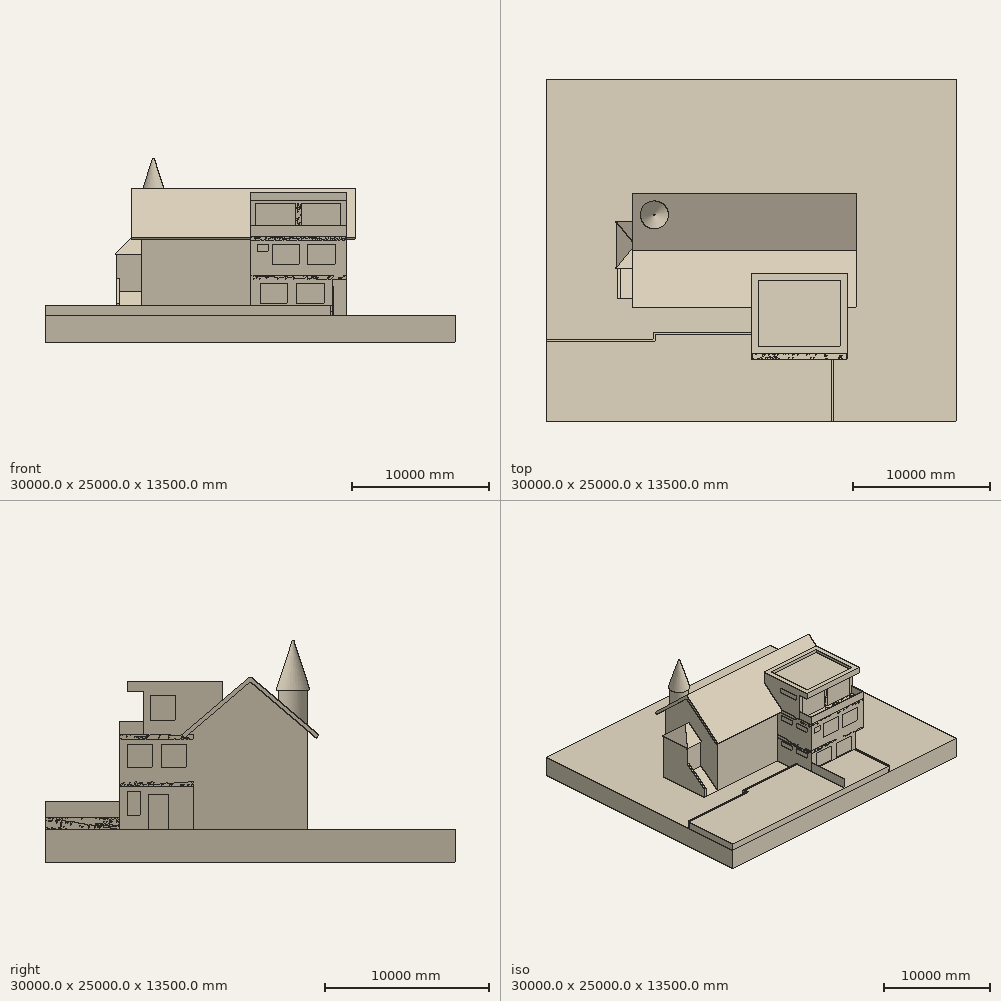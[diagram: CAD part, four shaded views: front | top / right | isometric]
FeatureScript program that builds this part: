
annotation { "Feature Type Name" : "Feature", "Feature Type Description" : "" }
export const myFeature = defineFeature(function(context is Context, id is Id, definition is map)
    precondition{}
    {
        {
            var Q0;
            Q0=qCreatedBy(makeId("Top.planeOp"),FACE);
            var sketch = newSketch(context, id + "F0", { "sketchPlane" : qUnion([Q0])});
            skLineSegment(sketch, "E0.bottom", {"start": v(-7000, 3500) * mm, "end": v(7000, 3500) * mm});
            skLineSegment(sketch, "E0.top", {"start": v(-7000, -3500) * mm, "end": v(7000, -3500) * mm});
            skLineSegment(sketch, "E0.left", {"start": v(-7000, 3500) * mm, "end": v(-7000, -3500) * mm});
            skLineSegment(sketch, "E0.right", {"start": v(7000, 3500) * mm, "end": v(7000, -3500) * mm});
            skPoint(sketch, "E0.middle", {"position": v(0, 0) * mm});
            skSolve(sketch);
        }
        {
            var Q0;
            Q0=makeQuery(id+"F0.imprint","IMPRINT",FACE,{"disambiguationData":[TD([[makeQuery(id+"F0.imprint","IMPRINT",EDGE,{"derivedFrom":sQuery(id+"F0.wireOp",EDGE,"E0.bottom")}),-1.0]])]});
            extrude(context, id + "F1", {"entities" : qUnion([Q0]), "depth" : 6000 * mm});
        }
        {
            var Q0;
            Q0=makeQuery(id+"F1.opExtrude","SWEPT_FACE",FACE,{"disambiguationData":[OSD([sQuery(id+"F0.wireOp",EDGE,"E0.left")])]});
            var sketch = newSketch(context, id + "F2", { "sketchPlane" : qUnion([Q0])});
            skLineSegment(sketch, "E1", {"start": v(0, 6000) * mm, "end": v(0, 8988.26) * mm});
            skPoint(sketch, "E1.endSnap0", {"position": v(0, 6000) * mm});
            skLineSegment(sketch, "E2", {"start": v(0, 8988.26) * mm, "end": v(-3500, 6000) * mm});
            skLineSegment(sketch, "E3", {"start": v(0, 8988.26) * mm, "end": v(3500, 6000) * mm});
            skSolve(sketch);
        }
        {
            var Q0;
            {var subQ0=sQuery(id+"F2.wireOp",EDGE,"E1");Q0=makeQuery(id+"F2.imprint","IMPRINT",FACE,{"disambiguationData":[TD([[makeQuery(id+"F2.imprint","IMPRINT",EDGE,{"derivedFrom":subQ0}),1.0]])]});}
            var Q1;
            {var subQ0=sQuery(id+"F2.wireOp",EDGE,"E1");Q1=makeQuery(id+"F2.imprint","IMPRINT",FACE,{"disambiguationData":[TD([[makeQuery(id+"F2.imprint","IMPRINT",EDGE,{"derivedFrom":subQ0}),-1.0]])]});}
            extrude(context, id + "F3", {"entities" : qUnion([Q0, Q1]), "operationType" : NewBodyOperationType.ADD, "oppositeDirection" : true, "depth" : 14000 * mm});
        }
        {
            var Q0;
            Q0=makeQuery(id+"F3.opExtrude","SWEPT_FACE",FACE,{"disambiguationData":[OSD([sQuery(id+"F2.wireOp",EDGE,"E2")])]});
            extrude(context, id + "F4", {"entities" : qUnion([Q0]), "operationType" : NewBodyOperationType.ADD, "endBound" : BoundingType.SYMMETRIC, "depth" : 500 * mm});
        }
        {
            var Q0;
            Q0=makeQuery(id+"F3.opExtrude","SWEPT_FACE",FACE,{"disambiguationData":[OSD([sQuery(id+"F2.wireOp",EDGE,"E3")])]});
            extrude(context, id + "F5", {"entities" : qUnion([Q0]), "operationType" : NewBodyOperationType.ADD, "endBound" : BoundingType.SYMMETRIC, "depth" : 500 * mm});
        }
        {
            var Q0;
            {var subQ0=sQuery(id+"F2.wireOp",EDGE,"E3");var subQ1=sQuery(id+"F2.wireOp",EDGE,"E2");var subQ2=sQuery(id+"F0.wireOp",EDGE,"E0.left");Q0=makeQuery(id+"F5.boolean.opBoolean","MERGE",FACE,{"derivedFrom":[makeQuery(id+"F4.boolean.opBoolean","MERGE",FACE,{"derivedFrom":[makeQuery(id+"F3.boolean.opBoolean","MERGE",FACE,{"derivedFrom":[makeQuery(id+"F1.opExtrude","SWEPT_FACE",FACE,{"disambiguationData":[OSD([subQ2])]}),makeQuery(id+"F3.opExtrude","CAP_FACE",FACE,{"disambiguationData":[OSD([subQ2,subQ1,subQ0])],"isStart":true})]}),makeQuery(id+"F4.opExtrude","SWEPT_FACE",FACE,{"disambiguationData":[OSD([subQ1]),TDD([makeQuery(id+"F3.opExtrude","CAP_EDGE",EDGE,{"disambiguationData":[OSD([subQ1])],"isStart":true})])]})]}),makeQuery(id+"F5.opExtrude","SWEPT_FACE",FACE,{"disambiguationData":[OSD([subQ0]),TDD([makeQuery(id+"F3.opExtrude","CAP_EDGE",EDGE,{"disambiguationData":[OSD([subQ0])],"isStart":true})])]})]});}
            var sketch = newSketch(context, id + "F6", { "sketchPlane" : qUnion([Q0])});
            skLineSegment(sketch, "E4", {"start": v(-162.33, 9178.39) * mm, "end": v(0, 9316.98) * mm});
            skLineSegment(sketch, "E5", {"start": v(0, 9316.98) * mm, "end": v(162.33, 9178.39) * mm});
            skSolve(sketch);
        }
        {
            var Q0;
            Q0=makeQuery(id+"F6.imprint","IMPRINT",FACE,{"disambiguationData":[TD([[makeQuery(id+"F6.imprint","IMPRINT",EDGE,{"derivedFrom":sQuery(id+"F6.wireOp",EDGE,"E4")}),-1.0]])]});
            extrude(context, id + "F7", {"entities" : qUnion([Q0]), "operationType" : NewBodyOperationType.ADD, "oppositeDirection" : true, "depth" : 14000 * mm});
        }
        {
            var Q0;
            Q0=makeQuery(id+"F4.opExtrude","SWEPT_FACE",FACE,{"disambiguationData":[OSD([sQuery(id+"F0.wireOp",EDGE,"E0.bottom"),sQuery(id+"F0.wireOp",EDGE,"E0.left"),sQuery(id+"F2.wireOp",EDGE,"E2")])]});
            extrude(context, id + "F8", {"entities" : qUnion([Q0]), "operationType" : NewBodyOperationType.ADD, "depth" : 700 * mm});
        }
        {
            var Q0;
            Q0=makeQuery(id+"F5.opExtrude","SWEPT_FACE",FACE,{"disambiguationData":[OSD([sQuery(id+"F0.wireOp",EDGE,"E0.top"),sQuery(id+"F0.wireOp",EDGE,"E0.left"),sQuery(id+"F2.wireOp",EDGE,"E3")])]});
            extrude(context, id + "F9", {"entities" : qUnion([Q0]), "operationType" : NewBodyOperationType.ADD, "depth" : 700 * mm});
        }
        {
            var Q0;
            {var subQ0=sQuery(id+"F2.wireOp",EDGE,"E3");var subQ1=sQuery(id+"F0.wireOp",EDGE,"E0.left");var subQ2=sQuery(id+"F0.wireOp",EDGE,"E0.top");var subQ3=sQuery(id+"F2.wireOp",EDGE,"E2");var subQ4=sQuery(id+"F0.wireOp",EDGE,"E0.bottom");Q0=makeQuery(id+"F9.boolean.opBoolean","MERGE",FACE,{"derivedFrom":[makeQuery(id+"F8.boolean.opBoolean","MERGE",FACE,{"derivedFrom":[makeQuery(id+"F7.boolean.opBoolean","MERGE",FACE,{"derivedFrom":[makeQuery(id+"F5.boolean.opBoolean","MERGE",FACE,{"derivedFrom":[makeQuery(id+"F4.boolean.opBoolean","MERGE",FACE,{"derivedFrom":[makeQuery(id+"F3.boolean.opBoolean","MERGE",FACE,{"derivedFrom":[makeQuery(id+"F1.opExtrude","SWEPT_FACE",FACE,{"disambiguationData":[OSD([subQ1])]}),makeQuery(id+"F3.opExtrude","CAP_FACE",FACE,{"disambiguationData":[OSD([subQ1,subQ3,subQ0])],"isStart":true})]}),makeQuery(id+"F4.opExtrude","SWEPT_FACE",FACE,{"disambiguationData":[OSD([subQ3]),TDD([makeQuery(id+"F3.opExtrude","CAP_EDGE",EDGE,{"disambiguationData":[OSD([subQ3])],"isStart":true})])]})]}),makeQuery(id+"F5.opExtrude","SWEPT_FACE",FACE,{"disambiguationData":[OSD([subQ0]),TDD([makeQuery(id+"F3.opExtrude","CAP_EDGE",EDGE,{"disambiguationData":[OSD([subQ0])],"isStart":true})])]})]}),makeQuery(id+"F7.opExtrude","CAP_FACE",FACE,{"disambiguationData":[OSD([sQuery(id+"F2.wireOp",EDGE,"E1"),subQ3,subQ0,sQuery(id+"F6.wireOp",EDGE,"E4"),sQuery(id+"F6.wireOp",EDGE,"E5")])],"isStart":true})]}),makeQuery(id+"F8.opExtrude","SWEPT_FACE",FACE,{"disambiguationData":[OSD([subQ4,subQ1,subQ3]),TDD([makeQuery(id+"F4.opExtrude","SWEPT_EDGE",EDGE,{"disambiguationData":[OSD([subQ4,subQ1,subQ3])]})])]})]}),makeQuery(id+"F9.opExtrude","SWEPT_FACE",FACE,{"disambiguationData":[OSD([subQ2,subQ1,subQ0]),TDD([makeQuery(id+"F5.opExtrude","SWEPT_EDGE",EDGE,{"disambiguationData":[OSD([subQ2,subQ1,subQ0])]})])]})]});}
            var sketch = newSketch(context, id + "F10", { "sketchPlane" : qUnion([Q0])});
            skLineSegment(sketch, "E6", {"start": v(-3500, 6000) * mm, "end": v(0, 8917.56) * mm});
            skLineSegment(sketch, "E7", {"start": v(0, 8917.56) * mm, "end": v(3500, 6000) * mm});
            skSolve(sketch);
        }
        {
            var Q0;
            Q0=makeQuery(id+"F10.imprint","IMPRINT",FACE,{"disambiguationData":[TD([[makeQuery(id+"F10.imprint","IMPRINT",EDGE,{"derivedFrom":sQuery(id+"F10.wireOp",EDGE,"E6")}),1.0]])]});
            extrude(context, id + "F11", {"entities" : qUnion([Q0]), "operationType" : NewBodyOperationType.ADD, "depth" : 700 * mm});
        }
        {
            var Q0;
            {var subQ0=sQuery(id+"F2.wireOp",EDGE,"E3");var subQ1=sQuery(id+"F0.wireOp",EDGE,"E0.right");var subQ2=sQuery(id+"F0.wireOp",EDGE,"E0.left");var subQ3=sQuery(id+"F2.wireOp",EDGE,"E2");Q0=makeQuery(id+"F9.boolean.opBoolean","MERGE",FACE,{"derivedFrom":[makeQuery(id+"F8.boolean.opBoolean","MERGE",FACE,{"derivedFrom":[makeQuery(id+"F7.boolean.opBoolean","MERGE",FACE,{"derivedFrom":[makeQuery(id+"F5.boolean.opBoolean","MERGE",FACE,{"derivedFrom":[makeQuery(id+"F4.boolean.opBoolean","MERGE",FACE,{"derivedFrom":[makeQuery(id+"F3.boolean.opBoolean","MERGE",FACE,{"derivedFrom":[makeQuery(id+"F1.opExtrude","SWEPT_FACE",FACE,{"disambiguationData":[OSD([subQ1])]}),makeQuery(id+"F3.opExtrude","CAP_FACE",FACE,{"disambiguationData":[OSD([subQ2,subQ3,subQ0])],"isStart":false})]}),makeQuery(id+"F4.opExtrude","SWEPT_FACE",FACE,{"disambiguationData":[OSD([subQ3]),TDD([makeQuery(id+"F3.opExtrude","CAP_EDGE",EDGE,{"disambiguationData":[OSD([subQ3])],"isStart":false})])]})]}),makeQuery(id+"F5.opExtrude","SWEPT_FACE",FACE,{"disambiguationData":[OSD([subQ0]),TDD([makeQuery(id+"F3.opExtrude","CAP_EDGE",EDGE,{"disambiguationData":[OSD([subQ0])],"isStart":false})])]})]}),makeQuery(id+"F7.opExtrude","CAP_FACE",FACE,{"disambiguationData":[OSD([sQuery(id+"F2.wireOp",EDGE,"E1"),subQ3,subQ0,sQuery(id+"F6.wireOp",EDGE,"E4"),sQuery(id+"F6.wireOp",EDGE,"E5")])],"isStart":false})]}),makeQuery(id+"F8.opExtrude","SWEPT_FACE",FACE,{"disambiguationData":[OSD([sQuery(id+"F0.wireOp",EDGE,"E0.bottom"),subQ2,subQ1,subQ3])]})]}),makeQuery(id+"F9.opExtrude","SWEPT_FACE",FACE,{"disambiguationData":[OSD([sQuery(id+"F0.wireOp",EDGE,"E0.top"),subQ2,subQ1,subQ0])]})]});}
            var sketch = newSketch(context, id + "F12", { "sketchPlane" : qUnion([Q0])});
            skLineSegment(sketch, "E8", {"start": v(-3500, 6000) * mm, "end": v(0, 8988.26) * mm});
            skLineSegment(sketch, "E9", {"start": v(0, 8988.26) * mm, "end": v(3500, 6000) * mm});
            skSolve(sketch);
        }
        {
            var Q0;
            Q0=makeQuery(id+"F12.imprint","IMPRINT",FACE,{"disambiguationData":[TD([[makeQuery(id+"F12.imprint","IMPRINT",EDGE,{"derivedFrom":sQuery(id+"F12.wireOp",EDGE,"E8")}),1.0]])]});
            extrude(context, id + "F13", {"entities" : qUnion([Q0]), "operationType" : NewBodyOperationType.ADD, "depth" : 700 * mm});
        }
        {
            var Q0;
            Q0=makeQuery(id+"F1.opExtrude","CAP_FACE",FACE,{"disambiguationData":[OSD([sQuery(id+"F0.wireOp",EDGE,"E0.bottom"),sQuery(id+"F0.wireOp",EDGE,"E0.top"),sQuery(id+"F0.wireOp",EDGE,"E0.left"),sQuery(id+"F0.wireOp",EDGE,"E0.right")])],"isStart":true});
            var sketch = newSketch(context, id + "F14", { "sketchPlane" : qUnion([Q0])});
            skLineSegment(sketch, "E10", {"start": v(7000, 3500) * mm, "end": v(0, 3500) * mm});
            skLineSegment(sketch, "E11", {"start": v(0, 3500) * mm, "end": v(0, 8000) * mm});
            skLineSegment(sketch, "E12", {"start": v(0, 8000) * mm, "end": v(7000, 8000) * mm});
            skLineSegment(sketch, "E13", {"start": v(7000, 8000) * mm, "end": v(7000, 3500) * mm});
            skSolve(sketch);
        }
        {
            var Q0;
            Q0=makeQuery(id+"F14.imprint","IMPRINT",FACE,{"disambiguationData":[TD([[makeQuery(id+"F14.imprint","IMPRINT",EDGE,{"derivedFrom":sQuery(id+"F14.wireOp",EDGE,"E10")}),1.0]])]});
            extrude(context, id + "F15", {"entities" : qUnion([Q0]), "operationType" : NewBodyOperationType.ADD, "oppositeDirection" : true, "depth" : 9000 * mm});
        }
        {
            var Q0;
            Q0=makeQuery(id+"F15.opExtrude","SWEPT_FACE",FACE,{"disambiguationData":[OSD([sQuery(id+"F14.wireOp",EDGE,"E10")])]});
            extrude(context, id + "F16", {"entities" : qUnion([Q0]), "operationType" : NewBodyOperationType.ADD, "depth" : 1800 * mm});
        }
        {
            var Q0;
            Q0=makeQuery(id+"F15.opExtrude","SWEPT_FACE",FACE,{"disambiguationData":[OSD([sQuery(id+"F14.wireOp",EDGE,"E12")])]});
            var sketch = newSketch(context, id + "F17", { "sketchPlane" : qUnion([Q0])});
            skLineSegment(sketch, "E14", {"start": v(0, 8400) * mm, "end": v(7000, 8400) * mm});
            skLineSegment(sketch, "E15", {"start": v(7000, 8400) * mm, "end": v(7000, 5800) * mm});
            skLineSegment(sketch, "E16", {"start": v(7000, 5800) * mm, "end": v(0, 5800) * mm});
            skLineSegment(sketch, "E17", {"start": v(0, 5800) * mm, "end": v(0, 8400) * mm});
            skSolve(sketch);
        }
        {
            var Q0;
            Q0=makeQuery(id+"F17.imprint","IMPRINT",FACE,{"disambiguationData":[TD([[makeQuery(id+"F17.imprint","IMPRINT",EDGE,{"derivedFrom":sQuery(id+"F17.wireOp",EDGE,"E14")}),-1.0]])]});
            extrude(context, id + "F18", {"entities" : qUnion([Q0]), "operationType" : NewBodyOperationType.REMOVE, "oppositeDirection" : true, "depth" : 1500 * mm, "offsetDistance" : 25 * mm});
        }
        {
            var Q0;
            {var subQ7=sQuery(id+"F14.wireOp",EDGE,"E10");var subQ8=sQuery(id+"F14.wireOp",EDGE,"E12");Q0=makeQuery(id+"F18.boolean.opBoolean","SPLIT",FACE,{"disambiguationData":[TD([makeQuery(id+"F16.opExtrude","SWEPT_FACE",FACE,{"disambiguationData":[OSD([subQ7])]})])],"derivedFrom":makeQuery(id+"F15.opExtrude","SWEPT_FACE",FACE,{"disambiguationData":[OSD([subQ8])]})});}
            extrude(context, id + "F19", {"entities" : qUnion([Q0]), "operationType" : NewBodyOperationType.REMOVE, "oppositeDirection" : true, "depth" : 500 * mm, "offsetDistance" : 25 * mm});
        }
        {
            var Q0;
            {var subQ0=sQuery(id+"F14.wireOp",EDGE,"E10");Q0=makeQuery(id+"F16.boolean.opBoolean","MERGE",FACE,{"derivedFrom":[makeQuery(id+"F15.opExtrude","CAP_FACE",FACE,{"disambiguationData":[OSD([subQ0,sQuery(id+"F14.wireOp",EDGE,"E11"),sQuery(id+"F14.wireOp",EDGE,"E12"),sQuery(id+"F14.wireOp",EDGE,"E13")])],"isStart":false}),makeQuery(id+"F16.opExtrude","SWEPT_FACE",FACE,{"disambiguationData":[OSD([subQ0])]})]});}
            var sketch = newSketch(context, id + "F20", { "sketchPlane" : qUnion([Q0])});
            skLineSegment(sketch, "E18", {"start": v(500, -2200) * mm, "end": v(500, -7000) * mm});
            skLineSegment(sketch, "E19", {"start": v(500, -7000) * mm, "end": v(6500, -7000) * mm});
            skLineSegment(sketch, "E20", {"start": v(6500, -7000) * mm, "end": v(6500, -2200) * mm});
            skLineSegment(sketch, "E21", {"start": v(6500, -2200) * mm, "end": v(500, -2200) * mm});
            skSolve(sketch);
        }
        {
            var Q0;
            Q0=makeQuery(id+"F20.imprint","IMPRINT",FACE,{"disambiguationData":[TD([[makeQuery(id+"F20.imprint","IMPRINT",EDGE,{"derivedFrom":sQuery(id+"F20.wireOp",EDGE,"E18")}),1.0]])]});
            extrude(context, id + "F21", {"entities" : qUnion([Q0]), "operationType" : NewBodyOperationType.REMOVE, "oppositeDirection" : true, "depth" : 300 * mm});
        }
        {
            var Q0;
            {var subQ1=sQuery(id+"F14.wireOp",EDGE,"E12");Q0=makeQuery(id+"F18.boolean.opBoolean","SPLIT",FACE,{"disambiguationData":[TD([makeQuery(id+"F18.opExtrude","SWEPT_FACE",FACE,{"disambiguationData":[OSD([sQuery(id+"F17.wireOp",EDGE,"E16")])]})])],"derivedFrom":makeQuery(id+"F15.opExtrude","SWEPT_FACE",FACE,{"disambiguationData":[OSD([subQ1])]})});}
            var sketch = newSketch(context, id + "F22", { "sketchPlane" : qUnion([Q0])});
            skLineSegment(sketch, "E22", {"start": v(0, 0) * mm, "end": v(7000, 0) * mm});
            skLineSegment(sketch, "E23", {"start": v(7000, 0) * mm, "end": v(7000, 2600) * mm});
            skLineSegment(sketch, "E24", {"start": v(7000, 2600) * mm, "end": v(0, 2600) * mm});
            skLineSegment(sketch, "E25", {"start": v(0, 2600) * mm, "end": v(0, 0) * mm});
            skLineSegment(sketch, "E26", {"start": v(0, 2600) * mm, "end": v(0, 2900) * mm});
            skLineSegment(sketch, "E27", {"start": v(7000, 2900) * mm, "end": v(7000, 2600) * mm});
            skLineSegment(sketch, "E28", {"start": v(0, 2900) * mm, "end": v(0, 5800) * mm});
            skLineSegment(sketch, "E29", {"start": v(0, 2900) * mm, "end": v(7000, 2900) * mm});
            skLineSegment(sketch, "E30", {"start": v(0, 2900) * mm, "end": v(0, 5500) * mm});
            skLineSegment(sketch, "E31", {"start": v(0, 5500) * mm, "end": v(7000, 5500) * mm});
            skLineSegment(sketch, "E32", {"start": v(7000, 5500) * mm, "end": v(7000, 2900) * mm});
            skLineSegment(sketch, "E33", {"start": v(0, 5800) * mm, "end": v(7000, 5800) * mm});
            skLineSegment(sketch, "E34", {"start": v(7000, 5800) * mm, "end": v(7000, 5500) * mm});
            skLineSegment(sketch, "E35", {"start": v(0, 5500) * mm, "end": v(0, 5800) * mm});
            skSolve(sketch);
        }
        {
            var Q0;
            Q0=makeQuery(id+"F22.imprint","IMPRINT",FACE,{"disambiguationData":[TD([[makeQuery(id+"F22.imprint","IMPRINT",EDGE,{"derivedFrom":sQuery(id+"F22.wireOp",EDGE,"E24")}),-1.0]])]});
            extrude(context, id + "F23", {"entities" : qUnion([Q0]), "oppositeDirection" : true, "depth" : 4500 * mm});
        }
        {
            var Q0;
            Q0=makeQuery(id+"F22.imprint","IMPRINT",FACE,{"disambiguationData":[TD([[makeQuery(id+"F22.imprint","IMPRINT",EDGE,{"derivedFrom":sQuery(id+"F22.wireOp",EDGE,"E31")}),1.0]])]});
            extrude(context, id + "F24", {"entities" : qUnion([Q0]), "oppositeDirection" : true, "depth" : 4500 * mm});
        }
        {
            var Q0;
            Q0=makeQuery(id+"F18.boolean.opBoolean","COPY",FACE,{"derivedFrom":makeQuery(id+"F18.opExtrude","SWEPT_FACE",FACE,{"disambiguationData":[OSD([sQuery(id+"F17.wireOp",EDGE,"E16")])]})});
            var sketch = newSketch(context, id + "F25", { "sketchPlane" : qUnion([Q0])});
            skLineSegment(sketch, "E36", {"start": v(40, -7960) * mm, "end": v(6960, -7960) * mm});
            skLineSegment(sketch, "E37", {"start": v(6960, -7960) * mm, "end": v(6960, -6500) * mm});
            skLineSegment(sketch, "E38", {"start": v(40, -6500) * mm, "end": v(40, -7960) * mm});
            skSolve(sketch);
        }
        {
            var Q0;
            Q0=makeQuery(id+"F25.imprint","IMPRINT",FACE,{"disambiguationData":[TD([[makeQuery(id+"F25.imprint","IMPRINT",EDGE,{"derivedFrom":sQuery(id+"F25.wireOp",EDGE,"E36")}),-1.0]])]});
            extrude(context, id + "F26", {"entities" : qUnion([Q0]), "depth" : 800 * mm});
        }
        {
            var Q0;
            {var subQ0=sQuery(id+"F14.wireOp",EDGE,"E13");var subQ1=sQuery(id+"F0.wireOp",EDGE,"E0.right");var subQ2=sQuery(id+"F2.wireOp",EDGE,"E3");var subQ3=sQuery(id+"F0.wireOp",EDGE,"E0.left");var subQ4=sQuery(id+"F2.wireOp",EDGE,"E2");Q0=makeQuery(id+"F16.boolean.opBoolean","MERGE",FACE,{"derivedFrom":[makeQuery(id+"F15.boolean.opBoolean","MERGE",FACE,{"derivedFrom":[makeQuery(id+"F9.boolean.opBoolean","MERGE",FACE,{"derivedFrom":[makeQuery(id+"F8.boolean.opBoolean","MERGE",FACE,{"derivedFrom":[makeQuery(id+"F7.boolean.opBoolean","MERGE",FACE,{"derivedFrom":[makeQuery(id+"F5.boolean.opBoolean","MERGE",FACE,{"derivedFrom":[makeQuery(id+"F4.boolean.opBoolean","MERGE",FACE,{"derivedFrom":[makeQuery(id+"F3.boolean.opBoolean","MERGE",FACE,{"derivedFrom":[makeQuery(id+"F1.opExtrude","SWEPT_FACE",FACE,{"disambiguationData":[OSD([subQ1])]}),makeQuery(id+"F3.opExtrude","CAP_FACE",FACE,{"disambiguationData":[OSD([subQ3,subQ4,subQ2])],"isStart":false})]}),makeQuery(id+"F4.opExtrude","SWEPT_FACE",FACE,{"disambiguationData":[OSD([subQ4]),TDD([makeQuery(id+"F3.opExtrude","CAP_EDGE",EDGE,{"disambiguationData":[OSD([subQ4])],"isStart":false})])]})]}),makeQuery(id+"F5.opExtrude","SWEPT_FACE",FACE,{"disambiguationData":[OSD([subQ2]),TDD([makeQuery(id+"F3.opExtrude","CAP_EDGE",EDGE,{"disambiguationData":[OSD([subQ2])],"isStart":false})])]})]}),makeQuery(id+"F7.opExtrude","CAP_FACE",FACE,{"disambiguationData":[OSD([sQuery(id+"F2.wireOp",EDGE,"E1"),subQ4,subQ2,sQuery(id+"F6.wireOp",EDGE,"E4"),sQuery(id+"F6.wireOp",EDGE,"E5")])],"isStart":false})]}),makeQuery(id+"F8.opExtrude","SWEPT_FACE",FACE,{"disambiguationData":[OSD([sQuery(id+"F0.wireOp",EDGE,"E0.bottom"),subQ3,subQ1,subQ4])]})]}),makeQuery(id+"F9.opExtrude","SWEPT_FACE",FACE,{"disambiguationData":[OSD([sQuery(id+"F0.wireOp",EDGE,"E0.top"),subQ3,subQ1,subQ2])]})]}),makeQuery(id+"F15.opExtrude","SWEPT_FACE",FACE,{"disambiguationData":[OSD([subQ0])]})]}),makeQuery(id+"F16.opExtrude","SWEPT_FACE",FACE,{"disambiguationData":[OSD([subQ1,sQuery(id+"F14.wireOp",EDGE,"E10"),subQ0])]})]});}
            var sketch = newSketch(context, id + "F27", { "sketchPlane" : qUnion([Q0])});
            skLineSegment(sketch, "E39", {"start": v(-8000, 0) * mm, "end": v(-8000, 2600.45) * mm});
            skLineSegment(sketch, "E40", {"start": v(-8000, 2600.45) * mm, "end": v(-3500, 2600.45) * mm});
            skLineSegment(sketch, "E41", {"start": v(-3500, 2600.45) * mm, "end": v(-3500, 0) * mm});
            skLineSegment(sketch, "E42", {"start": v(-3500, 0) * mm, "end": v(-8000, 0) * mm});
            skSolve(sketch);
        }
        {
            var Q0;
            Q0=makeQuery(id+"F27.imprint","IMPRINT",FACE,{"disambiguationData":[TD([[makeQuery(id+"F27.imprint","IMPRINT",EDGE,{"derivedFrom":sQuery(id+"F27.wireOp",EDGE,"E39")}),1.0]])]});
            extrude(context, id + "F28", {"entities" : qUnion([Q0]), "operationType" : NewBodyOperationType.REMOVE, "oppositeDirection" : true, "depth" : 1000 * mm});
        }
        {
            var Q0;
            {var subQ0=sQuery(id+"F27.wireOp",EDGE,"E40");var subQ1=sQuery(id+"F14.wireOp",EDGE,"E12");var subQ2=sQuery(id+"F27.wireOp",EDGE,"E41");Q0=makeQuery(id+"F28.boolean.opBoolean","COPY",FACE,{"disambiguationData":[TD([makeQuery(id+"F15.opExtrude","SWEPT_FACE",FACE,{"disambiguationData":[OSD([subQ1])]})])],"derivedFrom":makeQuery(id+"F28.opExtrude","CAP_FACE",FACE,{"disambiguationData":[OSD([sQuery(id+"F27.wireOp",EDGE,"E39"),subQ0,subQ2,sQuery(id+"F27.wireOp",EDGE,"E42")])],"isStart":false})});}
            var sketch = newSketch(context, id + "F29", { "sketchPlane" : qUnion([Q0])});
            skLineSegment(sketch, "E43", {"start": v(-6200, 0) * mm, "end": v(-6200, 2100) * mm});
            skLineSegment(sketch, "E44", {"start": v(-6200, 2100) * mm, "end": v(-5000, 2100) * mm});
            skLineSegment(sketch, "E45", {"start": v(-5000, 2100) * mm, "end": v(-5000, 0) * mm});
            skLineSegment(sketch, "E46", {"start": v(-5000, 0) * mm, "end": v(-6200, 0) * mm});
            skSolve(sketch);
        }
        {
            var Q0;
            Q0=makeQuery(id+"F29.imprint","IMPRINT",FACE,{"disambiguationData":[TD([[makeQuery(id+"F29.imprint","IMPRINT",EDGE,{"derivedFrom":sQuery(id+"F29.wireOp",EDGE,"E43")}),-1.0]])]});
            extrude(context, id + "F30", {"entities" : qUnion([Q0]), "endBound" : BoundingType.SYMMETRIC, "oppositeDirection" : true, "depth" : 100 * mm});
        }
        {
            var Q0;
            Q0=makeQuery(id+"F18.boolean.opBoolean","COPY",FACE,{"derivedFrom":makeQuery(id+"F18.opExtrude","CAP_FACE",FACE,{"disambiguationData":[OSD([sQuery(id+"F17.wireOp",EDGE,"E14"),sQuery(id+"F17.wireOp",EDGE,"E15"),sQuery(id+"F17.wireOp",EDGE,"E16"),sQuery(id+"F17.wireOp",EDGE,"E17")])],"isStart":false})});
            var sketch = newSketch(context, id + "F31", { "sketchPlane" : qUnion([Q0])});
            skLineSegment(sketch, "E47", {"start": v(348.69, 8181.2) * mm, "end": v(6584.02, 8181.2) * mm});
            skLineSegment(sketch, "E48", {"start": v(6584.02, 8181.2) * mm, "end": v(6584.02, 5800) * mm});
            skLineSegment(sketch, "E49", {"start": v(6584.02, 5800) * mm, "end": v(348.69, 5800) * mm});
            skLineSegment(sketch, "E50", {"start": v(348.69, 5800) * mm, "end": v(348.69, 8181.2) * mm});
            skSolve(sketch);
        }
        {
            var Q0;
            Q0 = qSketchRegion(id + "F31", true);
            extrude(context, id + "F32", {"entities" : qUnion([Q0]), "endBound" : BoundingType.SYMMETRIC, "oppositeDirection" : true, "depth" : 100 * mm});
        }
        {
            var Q0;
            Q0=makeQuery(id+"F18.boolean.opBoolean","COPY",FACE,{"derivedFrom":makeQuery(id+"F18.opExtrude","CAP_FACE",FACE,{"disambiguationData":[OSD([sQuery(id+"F17.wireOp",EDGE,"E14"),sQuery(id+"F17.wireOp",EDGE,"E15"),sQuery(id+"F17.wireOp",EDGE,"E16"),sQuery(id+"F17.wireOp",EDGE,"E17")])],"isStart":false})});
            var sketch = newSketch(context, id + "F33", { "sketchPlane" : qUnion([Q0])});
            skLineSegment(sketch, "E51", {"start": v(3300, 8400) * mm, "end": v(3300, 5800) * mm});
            skLineSegment(sketch, "E52", {"start": v(3300, 5800) * mm, "end": v(3700, 5800) * mm});
            skLineSegment(sketch, "E53", {"start": v(3700, 5800) * mm, "end": v(3700, 8400) * mm});
            skLineSegment(sketch, "E54", {"start": v(3700, 8400) * mm, "end": v(3300, 8400) * mm});
            skSolve(sketch);
        }
        {
            var Q0;
            Q0 = qSketchRegion(id + "F33", true);
            extrude(context, id + "F34", {"entities" : qUnion([Q0]), "operationType" : NewBodyOperationType.REMOVE, "depth" : 500 * mm});
        }
        {
            var Q0;
            {var subQ0=sQuery(id+"F14.wireOp",EDGE,"E11");Q0=makeQuery(id+"F16.boolean.opBoolean","MERGE",FACE,{"derivedFrom":[makeQuery(id+"F15.opExtrude","SWEPT_FACE",FACE,{"disambiguationData":[OSD([subQ0])]}),makeQuery(id+"F16.opExtrude","SWEPT_FACE",FACE,{"disambiguationData":[OSD([sQuery(id+"F0.wireOp",EDGE,"E0.top"),sQuery(id+"F14.wireOp",EDGE,"E10"),subQ0])]})]});}
            var sketch = newSketch(context, id + "F35", { "sketchPlane" : qUnion([Q0])});
            skLineSegment(sketch, "E55", {"start": v(6000, 2400) * mm, "end": v(7500, 2400) * mm});
            skLineSegment(sketch, "E56", {"start": v(7500, 2400) * mm, "end": v(7500, 1900) * mm});
            skLineSegment(sketch, "E57", {"start": v(7500, 1900) * mm, "end": v(6000, 1900) * mm});
            skLineSegment(sketch, "E58", {"start": v(6000, 1900) * mm, "end": v(6000, 2400) * mm});
            skLineSegment(sketch, "E59", {"start": v(5500, 2400) * mm, "end": v(4000, 2400) * mm});
            skLineSegment(sketch, "E60", {"start": v(4000, 2400) * mm, "end": v(4000, 1900) * mm});
            skLineSegment(sketch, "E61", {"start": v(4000, 1900) * mm, "end": v(5500, 1900) * mm});
            skLineSegment(sketch, "E62", {"start": v(5500, 1900) * mm, "end": v(5500, 2400) * mm});
            skSolve(sketch);
        }
        {
            var Q0;
            Q0=makeQuery(id+"F35.imprint","IMPRINT",FACE,{"disambiguationData":[TD([[makeQuery(id+"F35.imprint","IMPRINT",EDGE,{"derivedFrom":sQuery(id+"F35.wireOp",EDGE,"E55")}),-1.0]])]});
            var Q1;
            Q1=makeQuery(id+"F35.imprint","IMPRINT",FACE,{"disambiguationData":[TD([[makeQuery(id+"F35.imprint","IMPRINT",EDGE,{"derivedFrom":sQuery(id+"F35.wireOp",EDGE,"E59")}),1.0]])]});
            extrude(context, id + "F36", {"entities" : qUnion([Q0, Q1]), "endBound" : BoundingType.SYMMETRIC, "depth" : 10 * mm});
        }
        {
            var Q0;
            {var subQ1=sQuery(id+"F14.wireOp",EDGE,"E12");Q0=makeQuery(id+"F18.boolean.opBoolean","SPLIT",FACE,{"disambiguationData":[TD([makeQuery(id+"F18.opExtrude","SWEPT_FACE",FACE,{"disambiguationData":[OSD([sQuery(id+"F17.wireOp",EDGE,"E16")])]})])],"derivedFrom":makeQuery(id+"F15.opExtrude","SWEPT_FACE",FACE,{"disambiguationData":[OSD([subQ1])]})});}
            var sketch = newSketch(context, id + "F37", { "sketchPlane" : qUnion([Q0])});
            skLineSegment(sketch, "E63", {"start": v(700, 2350) * mm, "end": v(2700, 2350) * mm});
            skLineSegment(sketch, "E64", {"start": v(2700, 2350) * mm, "end": v(2700, 850) * mm});
            skLineSegment(sketch, "E65", {"start": v(2700, 850) * mm, "end": v(700, 850) * mm});
            skLineSegment(sketch, "E66", {"start": v(700, 850) * mm, "end": v(700, 2350) * mm});
            skLineSegment(sketch, "E67", {"start": v(3400, 2350) * mm, "end": v(5400, 2350) * mm});
            skLineSegment(sketch, "E68", {"start": v(5400, 2350) * mm, "end": v(5400, 850) * mm});
            skLineSegment(sketch, "E69", {"start": v(5400, 850) * mm, "end": v(3400, 850) * mm});
            skLineSegment(sketch, "E70", {"start": v(3400, 850) * mm, "end": v(3400, 2350) * mm});
            skSolve(sketch);
        }
        {
            var Q0;
            Q0 = qSketchRegion(id + "F37", true);
            extrude(context, id + "F38", {"entities" : qUnion([Q0]), "endBound" : BoundingType.SYMMETRIC, "depth" : 10 * mm});
        }
        {
            var Q0;
            {var subQ0=sQuery(id+"F14.wireOp",EDGE,"E11");Q0=makeQuery(id+"F16.boolean.opBoolean","MERGE",FACE,{"derivedFrom":[makeQuery(id+"F15.opExtrude","SWEPT_FACE",FACE,{"disambiguationData":[OSD([subQ0])]}),makeQuery(id+"F16.opExtrude","SWEPT_FACE",FACE,{"disambiguationData":[OSD([sQuery(id+"F0.wireOp",EDGE,"E0.top"),sQuery(id+"F14.wireOp",EDGE,"E10"),subQ0])]})]});}
            var sketch = newSketch(context, id + "F39", { "sketchPlane" : qUnion([Q0])});
            skLineSegment(sketch, "E71", {"start": v(4000, 5200) * mm, "end": v(4000, 4700) * mm});
            skLineSegment(sketch, "E72", {"start": v(4000, 4700) * mm, "end": v(5500, 4700) * mm});
            skLineSegment(sketch, "E73", {"start": v(5500, 4700) * mm, "end": v(5500, 5200) * mm});
            skLineSegment(sketch, "E74", {"start": v(5500, 5200) * mm, "end": v(4000, 5200) * mm});
            skLineSegment(sketch, "E75", {"start": v(6000, 5200) * mm, "end": v(6000, 4700) * mm});
            skLineSegment(sketch, "E76", {"start": v(6000, 4700) * mm, "end": v(7500, 4700) * mm});
            skLineSegment(sketch, "E77", {"start": v(7500, 4700) * mm, "end": v(7500, 5200) * mm});
            skLineSegment(sketch, "E78", {"start": v(7500, 5200) * mm, "end": v(6000, 5200) * mm});
            skSolve(sketch);
        }
        {
            var Q0;
            Q0 = qSketchRegion(id + "F39", true);
            extrude(context, id + "F40", {"entities" : qUnion([Q0]), "endBound" : BoundingType.SYMMETRIC, "depth" : 10 * mm});
        }
        {
            var Q0;
            {var subQ0=sQuery(id+"F27.wireOp",EDGE,"E40");var subQ1=sQuery(id+"F14.wireOp",EDGE,"E12");var subQ2=sQuery(id+"F27.wireOp",EDGE,"E41");Q0=makeQuery(id+"F28.boolean.opBoolean","COPY",FACE,{"disambiguationData":[TD([makeQuery(id+"F15.opExtrude","SWEPT_FACE",FACE,{"disambiguationData":[OSD([subQ1])]})])],"derivedFrom":makeQuery(id+"F28.opExtrude","CAP_FACE",FACE,{"disambiguationData":[OSD([sQuery(id+"F27.wireOp",EDGE,"E39"),subQ0,subQ2,sQuery(id+"F27.wireOp",EDGE,"E42")])],"isStart":false})});}
            var sketch = newSketch(context, id + "F41", { "sketchPlane" : qUnion([Q0])});
            skLineSegment(sketch, "E79", {"start": v(-7500, 2300.45) * mm, "end": v(-6700, 2300.45) * mm});
            skLineSegment(sketch, "E80", {"start": v(-6700, 2300.45) * mm, "end": v(-6700, 850) * mm});
            skLineSegment(sketch, "E81", {"start": v(-6700, 850) * mm, "end": v(-7500, 850) * mm});
            skLineSegment(sketch, "E82", {"start": v(-7500, 850) * mm, "end": v(-7500, 2300.45) * mm});
            skSolve(sketch);
        }
        {
            var Q0;
            Q0=makeQuery(id+"F41.imprint","IMPRINT",FACE,{"disambiguationData":[TD([[makeQuery(id+"F41.imprint","IMPRINT",EDGE,{"derivedFrom":sQuery(id+"F41.wireOp",EDGE,"E79")}),-1.0]])]});
            extrude(context, id + "F42", {"entities" : qUnion([Q0]), "endBound" : BoundingType.SYMMETRIC, "oppositeDirection" : true, "depth" : 10 * mm});
        }
        {
            var Q0;
            {var subQ1=sQuery(id+"F14.wireOp",EDGE,"E12");Q0=makeQuery(id+"F18.boolean.opBoolean","SPLIT",FACE,{"disambiguationData":[TD([makeQuery(id+"F18.opExtrude","SWEPT_FACE",FACE,{"disambiguationData":[OSD([sQuery(id+"F17.wireOp",EDGE,"E16")])]})])],"derivedFrom":makeQuery(id+"F15.opExtrude","SWEPT_FACE",FACE,{"disambiguationData":[OSD([subQ1])]})});}
            var sketch = newSketch(context, id + "F43", { "sketchPlane" : qUnion([Q0])});
            skLineSegment(sketch, "E83", {"start": v(500, 5200) * mm, "end": v(1300, 5200) * mm});
            skLineSegment(sketch, "E84", {"start": v(1300, 5200) * mm, "end": v(1300, 4700) * mm});
            skLineSegment(sketch, "E85", {"start": v(1300, 4700) * mm, "end": v(500, 4700) * mm});
            skLineSegment(sketch, "E86", {"start": v(500, 4700) * mm, "end": v(500, 5200) * mm});
            skLineSegment(sketch, "E87", {"start": v(1600, 5200) * mm, "end": v(1600, 3750) * mm});
            skLineSegment(sketch, "E88", {"start": v(1600, 3750) * mm, "end": v(3600, 3750) * mm});
            skLineSegment(sketch, "E89", {"start": v(3600, 3750) * mm, "end": v(3600, 5200) * mm});
            skLineSegment(sketch, "E90", {"start": v(3600, 5200) * mm, "end": v(1600, 5200) * mm});
            skLineSegment(sketch, "E91", {"start": v(4200, 5170.16) * mm, "end": v(6200, 5170.16) * mm});
            skLineSegment(sketch, "E92", {"start": v(6200, 5170.16) * mm, "end": v(6200, 3750) * mm});
            skLineSegment(sketch, "E93", {"start": v(6200, 3750) * mm, "end": v(4200, 3750) * mm});
            skLineSegment(sketch, "E94", {"start": v(4200, 3750) * mm, "end": v(4200, 5170.16) * mm});
            skSolve(sketch);
        }
        {
            var Q0;
            Q0 = qSketchRegion(id + "F43", true);
            extrude(context, id + "F44", {"entities" : qUnion([Q0]), "endBound" : BoundingType.SYMMETRIC, "depth" : 10 * mm});
        }
        {
            var Q0;
            {var subQ0=sQuery(id+"F14.wireOp",EDGE,"E13");var subQ1=sQuery(id+"F0.wireOp",EDGE,"E0.right");var subQ2=sQuery(id+"F2.wireOp",EDGE,"E3");var subQ3=sQuery(id+"F0.wireOp",EDGE,"E0.left");var subQ4=sQuery(id+"F2.wireOp",EDGE,"E2");Q0=makeQuery(id+"F16.boolean.opBoolean","MERGE",FACE,{"derivedFrom":[makeQuery(id+"F15.boolean.opBoolean","MERGE",FACE,{"derivedFrom":[makeQuery(id+"F9.boolean.opBoolean","MERGE",FACE,{"derivedFrom":[makeQuery(id+"F8.boolean.opBoolean","MERGE",FACE,{"derivedFrom":[makeQuery(id+"F7.boolean.opBoolean","MERGE",FACE,{"derivedFrom":[makeQuery(id+"F5.boolean.opBoolean","MERGE",FACE,{"derivedFrom":[makeQuery(id+"F4.boolean.opBoolean","MERGE",FACE,{"derivedFrom":[makeQuery(id+"F3.boolean.opBoolean","MERGE",FACE,{"derivedFrom":[makeQuery(id+"F1.opExtrude","SWEPT_FACE",FACE,{"disambiguationData":[OSD([subQ1])]}),makeQuery(id+"F3.opExtrude","CAP_FACE",FACE,{"disambiguationData":[OSD([subQ3,subQ4,subQ2])],"isStart":false})]}),makeQuery(id+"F4.opExtrude","SWEPT_FACE",FACE,{"disambiguationData":[OSD([subQ4]),TDD([makeQuery(id+"F3.opExtrude","CAP_EDGE",EDGE,{"disambiguationData":[OSD([subQ4])],"isStart":false})])]})]}),makeQuery(id+"F5.opExtrude","SWEPT_FACE",FACE,{"disambiguationData":[OSD([subQ2]),TDD([makeQuery(id+"F3.opExtrude","CAP_EDGE",EDGE,{"disambiguationData":[OSD([subQ2])],"isStart":false})])]})]}),makeQuery(id+"F7.opExtrude","CAP_FACE",FACE,{"disambiguationData":[OSD([sQuery(id+"F2.wireOp",EDGE,"E1"),subQ4,subQ2,sQuery(id+"F6.wireOp",EDGE,"E4"),sQuery(id+"F6.wireOp",EDGE,"E5")])],"isStart":false})]}),makeQuery(id+"F8.opExtrude","SWEPT_FACE",FACE,{"disambiguationData":[OSD([sQuery(id+"F0.wireOp",EDGE,"E0.bottom"),subQ3,subQ1,subQ4])]})]}),makeQuery(id+"F9.opExtrude","SWEPT_FACE",FACE,{"disambiguationData":[OSD([sQuery(id+"F0.wireOp",EDGE,"E0.top"),subQ3,subQ1,subQ2])]})]}),makeQuery(id+"F15.opExtrude","SWEPT_FACE",FACE,{"disambiguationData":[OSD([subQ0])]})]}),makeQuery(id+"F16.opExtrude","SWEPT_FACE",FACE,{"disambiguationData":[OSD([subQ1,sQuery(id+"F14.wireOp",EDGE,"E10"),subQ0])]})]});}
            var sketch = newSketch(context, id + "F45", { "sketchPlane" : qUnion([Q0])});
            skLineSegment(sketch, "E95", {"start": v(-7500, 5200) * mm, "end": v(-6000, 5200) * mm});
            skLineSegment(sketch, "E96", {"start": v(-6000, 5200) * mm, "end": v(-6000, 3750) * mm});
            skLineSegment(sketch, "E97", {"start": v(-6000, 3750) * mm, "end": v(-7500, 3750) * mm});
            skLineSegment(sketch, "E98", {"start": v(-7500, 3750) * mm, "end": v(-7500, 5200) * mm});
            skLineSegment(sketch, "E99", {"start": v(-5400, 5200) * mm, "end": v(-3900, 5200) * mm});
            skLineSegment(sketch, "E100", {"start": v(-3900, 5200) * mm, "end": v(-3900, 3750) * mm});
            skLineSegment(sketch, "E101", {"start": v(-3900, 3750) * mm, "end": v(-5400, 3750) * mm});
            skLineSegment(sketch, "E102", {"start": v(-5400, 3750) * mm, "end": v(-5400, 5200) * mm});
            skSolve(sketch);
        }
        {
            var Q0;
            Q0 = qSketchRegion(id + "F45", true);
            extrude(context, id + "F46", {"entities" : qUnion([Q0]), "endBound" : BoundingType.SYMMETRIC, "depth" : 10 * mm});
        }
        {
            var Q0;
            {var subQ0=sQuery(id+"F14.wireOp",EDGE,"E13");var subQ1=sQuery(id+"F0.wireOp",EDGE,"E0.right");var subQ2=sQuery(id+"F2.wireOp",EDGE,"E3");var subQ3=sQuery(id+"F0.wireOp",EDGE,"E0.left");var subQ4=sQuery(id+"F2.wireOp",EDGE,"E2");Q0=makeQuery(id+"F16.boolean.opBoolean","MERGE",FACE,{"derivedFrom":[makeQuery(id+"F15.boolean.opBoolean","MERGE",FACE,{"derivedFrom":[makeQuery(id+"F9.boolean.opBoolean","MERGE",FACE,{"derivedFrom":[makeQuery(id+"F8.boolean.opBoolean","MERGE",FACE,{"derivedFrom":[makeQuery(id+"F7.boolean.opBoolean","MERGE",FACE,{"derivedFrom":[makeQuery(id+"F5.boolean.opBoolean","MERGE",FACE,{"derivedFrom":[makeQuery(id+"F4.boolean.opBoolean","MERGE",FACE,{"derivedFrom":[makeQuery(id+"F3.boolean.opBoolean","MERGE",FACE,{"derivedFrom":[makeQuery(id+"F1.opExtrude","SWEPT_FACE",FACE,{"disambiguationData":[OSD([subQ1])]}),makeQuery(id+"F3.opExtrude","CAP_FACE",FACE,{"disambiguationData":[OSD([subQ3,subQ4,subQ2])],"isStart":false})]}),makeQuery(id+"F4.opExtrude","SWEPT_FACE",FACE,{"disambiguationData":[OSD([subQ4]),TDD([makeQuery(id+"F3.opExtrude","CAP_EDGE",EDGE,{"disambiguationData":[OSD([subQ4])],"isStart":false})])]})]}),makeQuery(id+"F5.opExtrude","SWEPT_FACE",FACE,{"disambiguationData":[OSD([subQ2]),TDD([makeQuery(id+"F3.opExtrude","CAP_EDGE",EDGE,{"disambiguationData":[OSD([subQ2])],"isStart":false})])]})]}),makeQuery(id+"F7.opExtrude","CAP_FACE",FACE,{"disambiguationData":[OSD([sQuery(id+"F2.wireOp",EDGE,"E1"),subQ4,subQ2,sQuery(id+"F6.wireOp",EDGE,"E4"),sQuery(id+"F6.wireOp",EDGE,"E5")])],"isStart":false})]}),makeQuery(id+"F8.opExtrude","SWEPT_FACE",FACE,{"disambiguationData":[OSD([sQuery(id+"F0.wireOp",EDGE,"E0.bottom"),subQ3,subQ1,subQ4])]})]}),makeQuery(id+"F9.opExtrude","SWEPT_FACE",FACE,{"disambiguationData":[OSD([sQuery(id+"F0.wireOp",EDGE,"E0.top"),subQ3,subQ1,subQ2])]})]}),makeQuery(id+"F15.opExtrude","SWEPT_FACE",FACE,{"disambiguationData":[OSD([subQ0])]})]}),makeQuery(id+"F16.opExtrude","SWEPT_FACE",FACE,{"disambiguationData":[OSD([subQ1,sQuery(id+"F14.wireOp",EDGE,"E10"),subQ0])]})]});}
            var sketch = newSketch(context, id + "F47", { "sketchPlane" : qUnion([Q0])});
            skLineSegment(sketch, "E103", {"start": v(-6100, 8180) * mm, "end": v(-4600, 8180) * mm});
            skLineSegment(sketch, "E104", {"start": v(-4600, 8180) * mm, "end": v(-4600, 6650) * mm});
            skLineSegment(sketch, "E105", {"start": v(-4600, 6650) * mm, "end": v(-6100, 6650) * mm});
            skLineSegment(sketch, "E106", {"start": v(-6100, 6650) * mm, "end": v(-6100, 8180) * mm});
            skSolve(sketch);
        }
        {
            var Q0;
            Q0 = qSketchRegion(id + "F47", true);
            extrude(context, id + "F48", {"entities" : qUnion([Q0]), "endBound" : BoundingType.SYMMETRIC, "depth" : 10 * mm});
        }
        {
            var Q0;
            {var subQ0=sQuery(id+"F14.wireOp",EDGE,"E11");Q0=makeQuery(id+"F16.boolean.opBoolean","MERGE",FACE,{"derivedFrom":[makeQuery(id+"F15.opExtrude","SWEPT_FACE",FACE,{"disambiguationData":[OSD([subQ0])]}),makeQuery(id+"F16.opExtrude","SWEPT_FACE",FACE,{"disambiguationData":[OSD([sQuery(id+"F0.wireOp",EDGE,"E0.top"),sQuery(id+"F14.wireOp",EDGE,"E10"),subQ0])]})]});}
            var sketch = newSketch(context, id + "F49", { "sketchPlane" : qUnion([Q0])});
            skLineSegment(sketch, "E107", {"start": v(6100, 8181.2) * mm, "end": v(3900, 8181.2) * mm});
            skLineSegment(sketch, "E108", {"start": v(3900, 8181.2) * mm, "end": v(3900, 7681.2) * mm});
            skLineSegment(sketch, "E109", {"start": v(3900, 7681.2) * mm, "end": v(6100, 7681.2) * mm});
            skLineSegment(sketch, "E110", {"start": v(6100, 7681.2) * mm, "end": v(6100, 8181.2) * mm});
            skSolve(sketch);
        }
        {
            var Q0;
            Q0 = qSketchRegion(id + "F49", true);
            extrude(context, id + "F50", {"entities" : qUnion([Q0]), "endBound" : BoundingType.SYMMETRIC, "depth" : 10 * mm});
        }
        {
            var Q0;
            Q0=makeQuery(id+"F15.boolean.opBoolean","MERGE",FACE,{"derivedFrom":[makeQuery(id+"F1.opExtrude","CAP_FACE",FACE,{"disambiguationData":[OSD([sQuery(id+"F0.wireOp",EDGE,"E0.bottom"),sQuery(id+"F0.wireOp",EDGE,"E0.top"),sQuery(id+"F0.wireOp",EDGE,"E0.left"),sQuery(id+"F0.wireOp",EDGE,"E0.right")])],"isStart":true}),makeQuery(id+"F15.opExtrude","CAP_FACE",FACE,{"disambiguationData":[OSD([sQuery(id+"F14.wireOp",EDGE,"E10"),sQuery(id+"F14.wireOp",EDGE,"E11"),sQuery(id+"F14.wireOp",EDGE,"E12"),sQuery(id+"F14.wireOp",EDGE,"E13")])],"isStart":true})]});
            var sketch = newSketch(context, id + "F51", { "sketchPlane" : qUnion([Q0])});
            skLineSegment(sketch, "E111.bottom", {"start": v(-15000, -12500) * mm, "end": v(15000, -12500) * mm});
            skLineSegment(sketch, "E111.top", {"start": v(-15000, 12500) * mm, "end": v(15000, 12500) * mm});
            skLineSegment(sketch, "E111.left", {"start": v(-15000, -12500) * mm, "end": v(-15000, 12500) * mm});
            skLineSegment(sketch, "E111.right", {"start": v(15000, -12500) * mm, "end": v(15000, 12500) * mm});
            skPoint(sketch, "E111.middle", {"position": v(0, 0) * mm});
            skSolve(sketch);
        }
        {
            var Q0;
            Q0 = qSketchRegion(id + "F51", true);
            extrude(context, id + "F52", {"entities" : qUnion([Q0]), "depth" : 2000 * mm});
        }
        {
            var Q0;
            Q0=makeQuery(id+"F52.opExtrude","CAP_FACE",FACE,{"disambiguationData":[OSD([sQuery(id+"F51.wireOp",EDGE,"E111.bottom"),sQuery(id+"F51.wireOp",EDGE,"E111.top"),sQuery(id+"F51.wireOp",EDGE,"E111.left"),sQuery(id+"F51.wireOp",EDGE,"E111.right")])],"isStart":true});
            var sketch = newSketch(context, id + "F53", { "sketchPlane" : qUnion([Q0])});
            skLineSegment(sketch, "E112", {"start": v(0, -6000) * mm, "end": v(-7000, -6000) * mm});
            skLineSegment(sketch, "E113", {"start": v(-7000, -6000) * mm, "end": v(-7000, -6150) * mm});
            skLineSegment(sketch, "E114", {"start": v(-7000, -6150) * mm, "end": v(0, -6150) * mm});
            skLineSegment(sketch, "E115", {"start": v(0, -6150) * mm, "end": v(0, -6000) * mm});
            skLineSegment(sketch, "E116", {"start": v(-7000, -6000) * mm, "end": v(-7000, -6650) * mm});
            skLineSegment(sketch, "E117", {"start": v(-7000, -6650) * mm, "end": v(-15000, -6650) * mm});
            skLineSegment(sketch, "E118", {"start": v(-15000, -6650) * mm, "end": v(-15000, -6500) * mm});
            skLineSegment(sketch, "E119", {"start": v(-15000, -6500) * mm, "end": v(-7150, -6500) * mm});
            skLineSegment(sketch, "E120", {"start": v(-7150, -6500) * mm, "end": v(-7150, -6000) * mm});
            skLineSegment(sketch, "E121", {"start": v(-7150, -6000) * mm, "end": v(-7000, -6000) * mm});
            skLineSegment(sketch, "E122", {"start": v(6000, -7999.08) * mm, "end": v(6000, -12500) * mm});
            skLineSegment(sketch, "E123", {"start": v(6000, -12500) * mm, "end": v(5850, -12500) * mm});
            skLineSegment(sketch, "E124", {"start": v(5850, -12500) * mm, "end": v(5850, -7999.08) * mm});
            skLineSegment(sketch, "E125", {"start": v(5850, -7999.08) * mm, "end": v(6000, -7999.08) * mm});
            skLineSegment(sketch, "E126", {"start": v(-15000, -6650) * mm, "end": v(-15000, -12500) * mm});
            skLineSegment(sketch, "E127", {"start": v(-15000, -12500) * mm, "end": v(5850, -12500) * mm});
            skLineSegment(sketch, "E128", {"start": v(5850, -7999.08) * mm, "end": v(0, -7999.08) * mm});
            skLineSegment(sketch, "E129", {"start": v(0, -7999.08) * mm, "end": v(0, -6150) * mm});
            skLineSegment(sketch, "E130", {"start": v(-7000, -6150) * mm, "end": v(-7000, -6650) * mm});
            skSolve(sketch);
        }
        {
            var Q0;
            Q0=makeQuery(id+"F53.imprint","IMPRINT",FACE,{"disambiguationData":[TD([[makeQuery(id+"F53.imprint","IMPRINT",EDGE,{"derivedFrom":sQuery(id+"F53.wireOp",EDGE,"E122")}),-1.0]])]});
            var Q1;
            Q1=makeQuery(id+"F53.imprint","IMPRINT",FACE,{"disambiguationData":[TD([[makeQuery(id+"F53.imprint","IMPRINT",EDGE,{"derivedFrom":sQuery(id+"F53.wireOp",EDGE,"E112")}),1.0]])]});
            var Q2;
            Q2=makeQuery(id+"F53.imprint","IMPRINT",FACE,{"disambiguationData":[TD([[makeQuery(id+"F53.imprint","IMPRINT",EDGE,{"derivedFrom":sQuery(id+"F53.wireOp",EDGE,"E116")}),-1.0]])]});
            extrude(context, id + "F54", {"entities" : qUnion([Q0, Q1, Q2]), "depth" : 750 * mm});
        }
        {
            var Q0;
            Q0 = qSketchRegion(id + "F53", true);
            extrude(context, id + "F55", {"entities" : qUnion([Q0]), "depth" : 700 * mm});
        }
        {
            var Q0;
            Q0=makeQuery(id+"F55.opExtrude","CAP_FACE",FACE,{"disambiguationData":[OSD([sQuery(id+"F53.wireOp",EDGE,"E112"),sQuery(id+"F53.wireOp",EDGE,"E115"),sQuery(id+"F53.wireOp",EDGE,"E118"),sQuery(id+"F53.wireOp",EDGE,"E119"),sQuery(id+"F53.wireOp",EDGE,"E120"),sQuery(id+"F53.wireOp",EDGE,"E121"),sQuery(id+"F53.wireOp",EDGE,"E122"),sQuery(id+"F53.wireOp",EDGE,"E123"),sQuery(id+"F53.wireOp",EDGE,"E125"),sQuery(id+"F53.wireOp",EDGE,"E126"),sQuery(id+"F53.wireOp",EDGE,"E127"),sQuery(id+"F53.wireOp",EDGE,"E128"),sQuery(id+"F53.wireOp",EDGE,"E129")])],"isStart":false});
            var sketch = newSketch(context, id + "F56", { "sketchPlane" : qUnion([Q0])});
            skLineSegment(sketch, "E131", {"start": v(0, -7999.08) * mm, "end": v(0, -12500) * mm});
            skLineSegment(sketch, "E132", {"start": v(0, -12500) * mm, "end": v(10, -12500) * mm});
            skLineSegment(sketch, "E133", {"start": v(10, -12500) * mm, "end": v(10, -7999.08) * mm});
            skLineSegment(sketch, "E134", {"start": v(10, -7999.08) * mm, "end": v(0, -7999.08) * mm});
            skSolve(sketch);
        }
        {
            var Q0;
            Q0 = qSketchRegion(id + "F56", true);
            extrude(context, id + "F57", {"entities" : qUnion([Q0]), "depth" : 1000 * mm});
        }
        {
            var Q0;
            {var subQ0=sQuery(id+"F2.wireOp",EDGE,"E3");var subQ1=sQuery(id+"F0.wireOp",EDGE,"E0.left");var subQ2=sQuery(id+"F0.wireOp",EDGE,"E0.top");var subQ3=sQuery(id+"F2.wireOp",EDGE,"E2");var subQ4=sQuery(id+"F0.wireOp",EDGE,"E0.bottom");Q0=makeQuery(id+"F9.boolean.opBoolean","MERGE",FACE,{"derivedFrom":[makeQuery(id+"F8.boolean.opBoolean","MERGE",FACE,{"derivedFrom":[makeQuery(id+"F7.boolean.opBoolean","MERGE",FACE,{"derivedFrom":[makeQuery(id+"F5.boolean.opBoolean","MERGE",FACE,{"derivedFrom":[makeQuery(id+"F4.boolean.opBoolean","MERGE",FACE,{"derivedFrom":[makeQuery(id+"F3.boolean.opBoolean","MERGE",FACE,{"derivedFrom":[makeQuery(id+"F1.opExtrude","SWEPT_FACE",FACE,{"disambiguationData":[OSD([subQ1])]}),makeQuery(id+"F3.opExtrude","CAP_FACE",FACE,{"disambiguationData":[OSD([subQ1,subQ3,subQ0])],"isStart":true})]}),makeQuery(id+"F4.opExtrude","SWEPT_FACE",FACE,{"disambiguationData":[OSD([subQ3]),TDD([makeQuery(id+"F3.opExtrude","CAP_EDGE",EDGE,{"disambiguationData":[OSD([subQ3])],"isStart":true})])]})]}),makeQuery(id+"F5.opExtrude","SWEPT_FACE",FACE,{"disambiguationData":[OSD([subQ0]),TDD([makeQuery(id+"F3.opExtrude","CAP_EDGE",EDGE,{"disambiguationData":[OSD([subQ0])],"isStart":true})])]})]}),makeQuery(id+"F7.opExtrude","CAP_FACE",FACE,{"disambiguationData":[OSD([sQuery(id+"F2.wireOp",EDGE,"E1"),subQ3,subQ0,sQuery(id+"F6.wireOp",EDGE,"E4"),sQuery(id+"F6.wireOp",EDGE,"E5")])],"isStart":true})]}),makeQuery(id+"F8.opExtrude","SWEPT_FACE",FACE,{"disambiguationData":[OSD([subQ4,subQ1,subQ3]),TDD([makeQuery(id+"F4.opExtrude","SWEPT_EDGE",EDGE,{"disambiguationData":[OSD([subQ4,subQ1,subQ3])]})])]})]}),makeQuery(id+"F9.opExtrude","SWEPT_FACE",FACE,{"disambiguationData":[OSD([subQ2,subQ1,subQ0]),TDD([makeQuery(id+"F5.opExtrude","SWEPT_EDGE",EDGE,{"disambiguationData":[OSD([subQ2,subQ1,subQ0])]})])]})]});}
            extrude(context, id + "F58", {"entities" : qUnion([Q0]), "operationType" : NewBodyOperationType.ADD, "depth" : 1000 * mm});
        }
        {
            var Q0;
            Q0=makeQuery(id+"F11.opExtrude","CAP_FACE",FACE,{"disambiguationData":[OSD([sQuery(id+"F0.wireOp",EDGE,"E0.bottom"),sQuery(id+"F0.wireOp",EDGE,"E0.top"),sQuery(id+"F0.wireOp",EDGE,"E0.left"),sQuery(id+"F2.wireOp",EDGE,"E2"),sQuery(id+"F2.wireOp",EDGE,"E3"),sQuery(id+"F6.wireOp",EDGE,"E4"),sQuery(id+"F6.wireOp",EDGE,"E5"),sQuery(id+"F10.wireOp",EDGE,"E6"),sQuery(id+"F10.wireOp",EDGE,"E7")])],"isStart":false});
            extrude(context, id + "F59", {"entities" : qUnion([Q0]), "operationType" : NewBodyOperationType.ADD, "depth" : 1000 * mm});
        }
        {
            var Q0;
            Q0=makeQuery(id+"F58.opExtrude","CAP_FACE",FACE,{"disambiguationData":[OSD([sQuery(id+"F0.wireOp",EDGE,"E0.bottom"),sQuery(id+"F0.wireOp",EDGE,"E0.top"),sQuery(id+"F0.wireOp",EDGE,"E0.left"),sQuery(id+"F2.wireOp",EDGE,"E1"),sQuery(id+"F2.wireOp",EDGE,"E2"),sQuery(id+"F2.wireOp",EDGE,"E3"),sQuery(id+"F6.wireOp",EDGE,"E4"),sQuery(id+"F6.wireOp",EDGE,"E5")])],"isStart":false});
            var sketch = newSketch(context, id + "F60", { "sketchPlane" : qUnion([Q0])});
            skLineSegment(sketch, "E135", {"start": v(3500, 0) * mm, "end": v(1224.48, 1777.83) * mm});
            skLineSegment(sketch, "E136", {"start": v(1224.48, 1777.83) * mm, "end": v(1224.48, 4500) * mm});
            skLineSegment(sketch, "E137", {"start": v(1224.48, 4500) * mm, "end": v(-2000, 4500) * mm});
            skLineSegment(sketch, "E138", {"start": v(-2000, 4500) * mm, "end": v(-2000, 0) * mm});
            skLineSegment(sketch, "E139", {"start": v(-2000, 0) * mm, "end": v(3500, 0) * mm});
            skSolve(sketch);
        }
        {
            var Q0;
            Q0=makeQuery(id+"F60.imprint","IMPRINT",FACE,{"disambiguationData":[TD([[makeQuery(id+"F60.imprint","IMPRINT",EDGE,{"derivedFrom":sQuery(id+"F60.wireOp",EDGE,"E135")}),1.0]])]});
            extrude(context, id + "F61", {"entities" : qUnion([Q0]), "operationType" : NewBodyOperationType.ADD, "depth" : 1800 * mm});
        }
        {
            var Q0;
            Q0=makeQuery(id+"F58.opExtrude","CAP_FACE",FACE,{"disambiguationData":[OSD([sQuery(id+"F0.wireOp",EDGE,"E0.bottom"),sQuery(id+"F0.wireOp",EDGE,"E0.top"),sQuery(id+"F0.wireOp",EDGE,"E0.left"),sQuery(id+"F2.wireOp",EDGE,"E1"),sQuery(id+"F2.wireOp",EDGE,"E2"),sQuery(id+"F2.wireOp",EDGE,"E3"),sQuery(id+"F6.wireOp",EDGE,"E4"),sQuery(id+"F6.wireOp",EDGE,"E5")])],"isStart":false});
            var sketch = newSketch(context, id + "F62", { "sketchPlane" : qUnion([Q0])});
            skPoint(sketch, "E140", {"position": v(-387.76, 4500) * mm});
            skPoint(sketch, "E141", {"position": v(-387.76, 5825.64) * mm});
            skLineSegment(sketch, "E142", {"start": v(-387.76, 5825.64) * mm, "end": v(1224.48, 4500) * mm});
            skLineSegment(sketch, "E143", {"start": v(1224.48, 4500) * mm, "end": v(-2000, 4500) * mm});
            skLineSegment(sketch, "E144", {"start": v(-2000, 4500) * mm, "end": v(-387.76, 5825.64) * mm});
            skSolve(sketch);
        }
        {
            var Q0;
            Q0=makeQuery(id+"F62.imprint","IMPRINT",FACE,{"disambiguationData":[TD([[makeQuery(id+"F62.imprint","IMPRINT",EDGE,{"derivedFrom":sQuery(id+"F62.wireOp",EDGE,"E142")}),-1.0]])]});
            extrude(context, id + "F63", {"entities" : qUnion([Q0]), "operationType" : NewBodyOperationType.ADD, "depth" : 2000 * mm});
        }
        {
            var Q0;
            Q0=makeQuery(id+"F63.opExtrude","SWEPT_FACE",FACE,{"disambiguationData":[OSD([sQuery(id+"F62.wireOp",EDGE,"E142")])]});
            extrude(context, id + "F64", {"entities" : qUnion([Q0]), "operationType" : NewBodyOperationType.ADD, "depth" : 50 * mm});
        }
        {
            var Q0;
            Q0=makeQuery(id+"F63.opExtrude","SWEPT_FACE",FACE,{"disambiguationData":[OSD([sQuery(id+"F62.wireOp",EDGE,"E144")])]});
            extrude(context, id + "F65", {"entities" : qUnion([Q0]), "operationType" : NewBodyOperationType.ADD, "depth" : 50 * mm});
        }
        {
            var Q0;
            {var subQ0=sQuery(id+"F62.wireOp",EDGE,"E144");var subQ1=sQuery(id+"F62.wireOp",EDGE,"E142");Q0=makeQuery(id+"F65.boolean.opBoolean","MERGE",FACE,{"derivedFrom":[makeQuery(id+"F64.boolean.opBoolean","MERGE",FACE,{"derivedFrom":[makeQuery(id+"F63.opExtrude","CAP_FACE",FACE,{"disambiguationData":[OSD([subQ1,sQuery(id+"F62.wireOp",EDGE,"E143"),subQ0])],"isStart":false}),makeQuery(id+"F64.opExtrude","SWEPT_FACE",FACE,{"disambiguationData":[OSD([subQ1]),TDD([makeQuery(id+"F63.opExtrude","CAP_EDGE",EDGE,{"disambiguationData":[OSD([subQ1])],"isStart":false})])]})]}),makeQuery(id+"F65.opExtrude","SWEPT_FACE",FACE,{"disambiguationData":[OSD([subQ0]),TDD([makeQuery(id+"F63.opExtrude","CAP_EDGE",EDGE,{"disambiguationData":[OSD([subQ0])],"isStart":false})])]})]});}
            var sketch = newSketch(context, id + "F66", { "sketchPlane" : qUnion([Q0])});
            skLineSegment(sketch, "E145", {"start": v(-419.52, 5864.26) * mm, "end": v(-387.76, 5890.37) * mm});
            skLineSegment(sketch, "E146", {"start": v(-387.76, 5890.37) * mm, "end": v(-356, 5864.26) * mm});
            skLineSegment(sketch, "E147", {"start": v(-356, 5864.26) * mm, "end": v(-387.76, 5825.64) * mm});
            skLineSegment(sketch, "E148", {"start": v(-387.76, 5825.64) * mm, "end": v(-419.52, 5864.26) * mm});
            skSolve(sketch);
        }
        {
            var Q0;
            Q0 = qSketchRegion(id + "F66", true);
            extrude(context, id + "F67", {"entities" : qUnion([Q0]), "operationType" : NewBodyOperationType.ADD, "oppositeDirection" : true, "depth" : 2000 * mm});
        }
        {
            var Q0;
            Q0=makeQuery(id+"F65.opExtrude","SWEPT_FACE",FACE,{"disambiguationData":[OSD([sQuery(id+"F60.wireOp",EDGE,"E137"),sQuery(id+"F60.wireOp",EDGE,"E138"),sQuery(id+"F62.wireOp",EDGE,"E143"),sQuery(id+"F62.wireOp",EDGE,"E144")])]});
            extrude(context, id + "F68", {"entities" : qUnion([Q0]), "operationType" : NewBodyOperationType.ADD, "depth" : 100 * mm});
        }
        {
            var Q0;
            Q0=makeQuery(id+"F64.opExtrude","SWEPT_FACE",FACE,{"disambiguationData":[OSD([sQuery(id+"F60.wireOp",EDGE,"E136"),sQuery(id+"F60.wireOp",EDGE,"E137"),sQuery(id+"F62.wireOp",EDGE,"E142"),sQuery(id+"F62.wireOp",EDGE,"E143")])]});
            extrude(context, id + "F69", {"entities" : qUnion([Q0]), "operationType" : NewBodyOperationType.ADD, "depth" : 100 * mm});
        }
        {
            var Q0;
            {var subQ0=sQuery(id+"F0.wireOp",EDGE,"E0.top");Q0=makeQuery(id+"F58.boolean.opBoolean","MERGE",FACE,{"derivedFrom":[makeQuery(id+"F1.opExtrude","SWEPT_FACE",FACE,{"disambiguationData":[OSD([subQ0])]}),makeQuery(id+"F58.opExtrude","SWEPT_FACE",FACE,{"disambiguationData":[OSD([subQ0,sQuery(id+"F0.wireOp",EDGE,"E0.left")])]})]});}
            var sketch = newSketch(context, id + "F70", { "sketchPlane" : qUnion([Q0])});
            skLineSegment(sketch, "E149", {"start": v(-8400, 5990.37) * mm, "end": v(-10200, 4190.37) * mm});
            skLineSegment(sketch, "E150", {"start": v(-10200, 4190.37) * mm, "end": v(-10200, 5990.37) * mm});
            skLineSegment(sketch, "E151", {"start": v(-10200, 5990.37) * mm, "end": v(-8400, 5990.37) * mm});
            skSolve(sketch);
        }
        {
            var Q0;
            Q0 = qSketchRegion(id + "F70", true);
            extrude(context, id + "F71", {"entities" : qUnion([Q0]), "operationType" : NewBodyOperationType.REMOVE, "oppositeDirection" : true, "depth" : 6000 * mm});
        }
        {
            var Q0;
            Q0=makeQuery(id+"F61.opExtrude","CAP_FACE",FACE,{"disambiguationData":[OSD([sQuery(id+"F60.wireOp",EDGE,"E135"),sQuery(id+"F60.wireOp",EDGE,"E136"),sQuery(id+"F60.wireOp",EDGE,"E137"),sQuery(id+"F60.wireOp",EDGE,"E138"),sQuery(id+"F60.wireOp",EDGE,"E139")])],"isStart":false});
            var sketch = newSketch(context, id + "F72", { "sketchPlane" : qUnion([Q0])});
            skLineSegment(sketch, "E152", {"start": v(1224.48, 1777.83) * mm, "end": v(1224.48, 2685.7) * mm});
            skLineSegment(sketch, "E153", {"start": v(1224.48, 2685.7) * mm, "end": v(3500, 907.87) * mm});
            skLineSegment(sketch, "E154", {"start": v(3500, 907.87) * mm, "end": v(3500, 0) * mm});
            skLineSegment(sketch, "E155", {"start": v(3500, 0) * mm, "end": v(1224.48, 1777.83) * mm});
            skSolve(sketch);
        }
        {
            var Q0;
            Q0 = qSketchRegion(id + "F72", true);
            extrude(context, id + "F73", {"entities" : qUnion([Q0]), "operationType" : NewBodyOperationType.ADD, "oppositeDirection" : true, "depth" : 200 * mm});
        }
        {
            var Q0;
            Q0=makeQuery(id+"F52.opExtrude","CAP_FACE",FACE,{"disambiguationData":[OSD([sQuery(id+"F51.wireOp",EDGE,"E111.bottom"),sQuery(id+"F51.wireOp",EDGE,"E111.top"),sQuery(id+"F51.wireOp",EDGE,"E111.left"),sQuery(id+"F51.wireOp",EDGE,"E111.right")])],"isStart":true});
            var sketch = newSketch(context, id + "F74", { "sketchPlane" : qUnion([Q0])});
            skLineSegment(sketch, "E156", {"start": v(-8000, 2600) * mm, "end": v(-7100, 2600) * mm, "construction": true});
            skCircle(sketch, "E157", {"center": v(-7100, 2600) * mm, "radius": 900 * mm});
            skSolve(sketch);
        }
        {
            var Q0;
            Q0 = qSketchRegion(id + "F74", true);
            extrude(context, id + "F75", {"entities" : qUnion([Q0]), "operationType" : NewBodyOperationType.ADD, "depth" : 8500 * mm});
        }
        {
            var Q0;
            Q0=makeQuery(id+"F75.opExtrude","CAP_FACE",FACE,{"disambiguationData":[OSD([sQuery(id+"F74.wireOp",EDGE,"E157")])],"isStart":false});
            var sketch = newSketch(context, id + "F76", { "sketchPlane" : qUnion([Q0])});
            skCircle(sketch, "E158", {"center": v(-7100, 2600) * mm, "radius": 1050 * mm});
            skSolve(sketch);
        }
        {
            var Q0;
            Q0 = qSketchRegion(id + "F76", true);
            extrude(context, id + "F77", {"entities" : qUnion([Q0]), "operationType" : NewBodyOperationType.ADD, "depth" : 3000 * mm});
        }
        {
            var Q0;
            Q0=makeQuery(id+"F77.opExtrude","CAP_EDGE",EDGE,{"disambiguationData":[OSD([sQuery(id+"F76.wireOp",EDGE,"E158")])],"isStart":false});
            chamfer(context, id + "F78", {"entities" : qUnion([Q0]), "chamferType" : ChamferType.OFFSET_ANGLE, "width" : 1000 * mm, "oppositeDirection" : false, "angle" : 72 * degree, "tangentPropagation" : true});
        }
    });
